# Revit family: LAMP_FIL 35 1400MM OPAL COMFORT TRIMLESS
name_source: partatom
category: Luminarias
revit_build: Autodesk Revit 2018 (Build: 20170223_1515(x64)
units: mm (PartAtom-declared; Revit-internal decimal feet)

## family parameters
Anfitrión = Cara
Compartido = No
Corte con vacíos al cargar = No
Cota de conector redondo = Diámetro de uso
Origen de luz = Sí
Punto de cálculo de habitación = No
Tipo de pieza = Normal

## types (4) — shared parameters
CRI = 80
Cambio de temperatura de color de luz atenuada = <Ninguno>
Dimensions = 1400x51x76
Elevación por defecto = 1219 mm
Fabricante = LAMP
Filtro de color = 16777215
Finish = Matte white RAL 9010
Gear = Electronic
IEE = A+
Installation instructions = https://www.lamp.es
Insulation class = I
LED Lifetime = 50.000 L90 B10
Lamp = MID-POWER LED
Last update = 07/05/2021
Longitud de línea de emisión = 1400 mm  [stored 4.59318 ft]
MacAdam = 3
Manufacturer URL = http://www.lamp.es
Manufacturer country = Spain
Manufacturer name = LAMP
Material difusor = LAMP_PC Difusor Opal Fil
Material perfil = LAMP_Aluminio Perfil Fil BL
Material suspension = LAMP_Acero genérico
Plum = 14 W
Power = 14 W
Power Supply = 220-240V 50/60Hz
Product URL = https://www.lamp.es
Product datasheet = http://www.lamp.es
Protection rating = IP20 / IK07
Recessed dimensions = 1407x52x0
Type = MID POWER TRIDONIC
Weight = 3.35 kg
Ángulo de inclinación = -90.00°

## per-type parameters (varying)
| type | Archivo de red fotométrica | Descripción | Efficacy | Modelo | Product code |
| 1334LM 3000K DALI WHITE | F31TR140LOOC830NW.IES | FIL35 TRIM 1400 2000 WW OP COMF DALI WH. | 93 lm/W | F31TR140LOOC830DW | F31TR140LOOC830DW |
| 1334LM 3000K  WHITE | F31TR140LOOC830NW.IES | FIL35 TRIM 1400 2000 WW OP COMF WH. | 93 lm/W | F31TR140LOOC830NW | F31TR140LOOC830NW |
| 1390LM 4000K DALI WHITE | F31TR140LOOC840nW.IES | FIL35 TRIM 1400 2000 NW OP COMF DALI WH. | 97 lm/W | F31TR140LOOC840DW | F31TR140LOOC840DW |
| 1390LM 4000K  WHITE | F31TR140LOOC840NW.IES | FIL35 TRIM 1400 2000 NW OP COMF WH. | 97 lm/W | F31TR140LOOC840NW | F31TR140LOOC840NW |

note: [stored X ft] marks values corroborated as IEEE doubles in the binary element streams (Revit-internal decimal feet)
